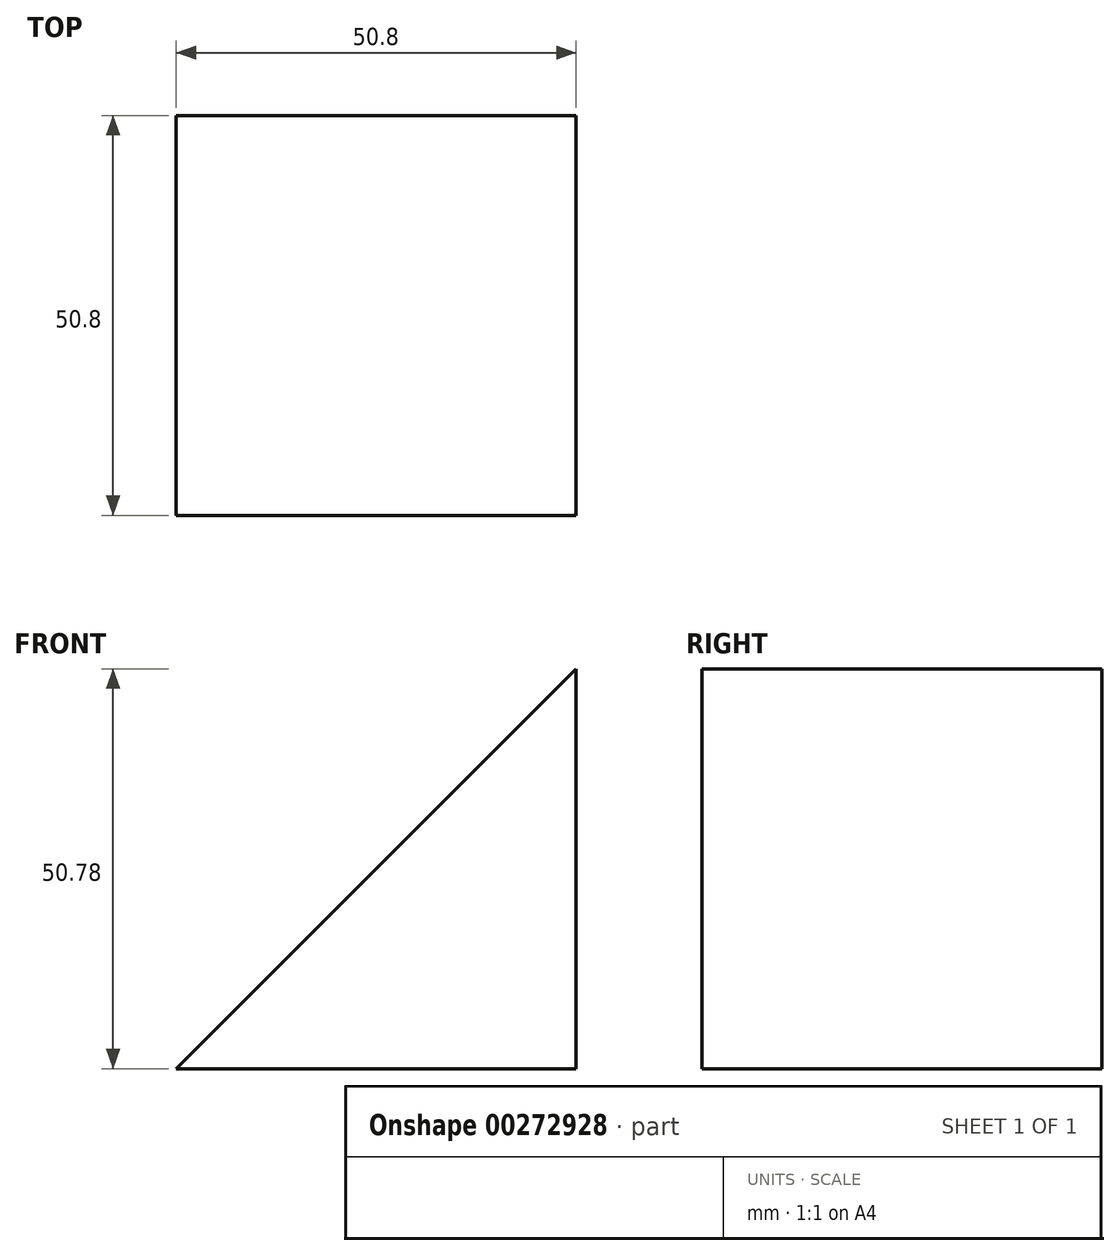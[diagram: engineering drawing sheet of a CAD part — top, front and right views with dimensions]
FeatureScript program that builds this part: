
annotation { "Feature Type Name" : "Feature", "Feature Type Description" : "" }
export const myFeature = defineFeature(function(context is Context, id is Id, definition is map)
    precondition{}
    {
        {
            var Q0;
            Q0=qCreatedBy(makeId("Front.planeOp"),FACE);
            var sketch = newSketch(context, id + "F0", { "sketchPlane" : qUnion([Q0])});
            skLineSegment(sketch, "E0", {"start": v(0, 0) * mm, "end": v(-50.8, 0) * mm});
            skLineSegment(sketch, "E1", {"start": v(0, -0.02) * mm, "end": v(0, 50.78) * mm});
            skLineSegment(sketch, "E2", {"start": v(0, 50.78) * mm, "end": v(-50.8, 0) * mm});
            skSolve(sketch);
        }
        {
            var Q0;
            {var subQ0=sQuery(id+"F0.wireOp",EDGE,"E0");Q0=makeQuery(id+"F0.imprint","IMPRINT",FACE,{"disambiguationData":[TD([[makeQuery(id+"F0.imprint","IMPRINT",EDGE,{"derivedFrom":subQ0}),-1.0]])]});}
            extrude(context, id + "F1", {"entities" : qUnion([Q0]), "depth" : 50.8 * mm});
        }
    });
